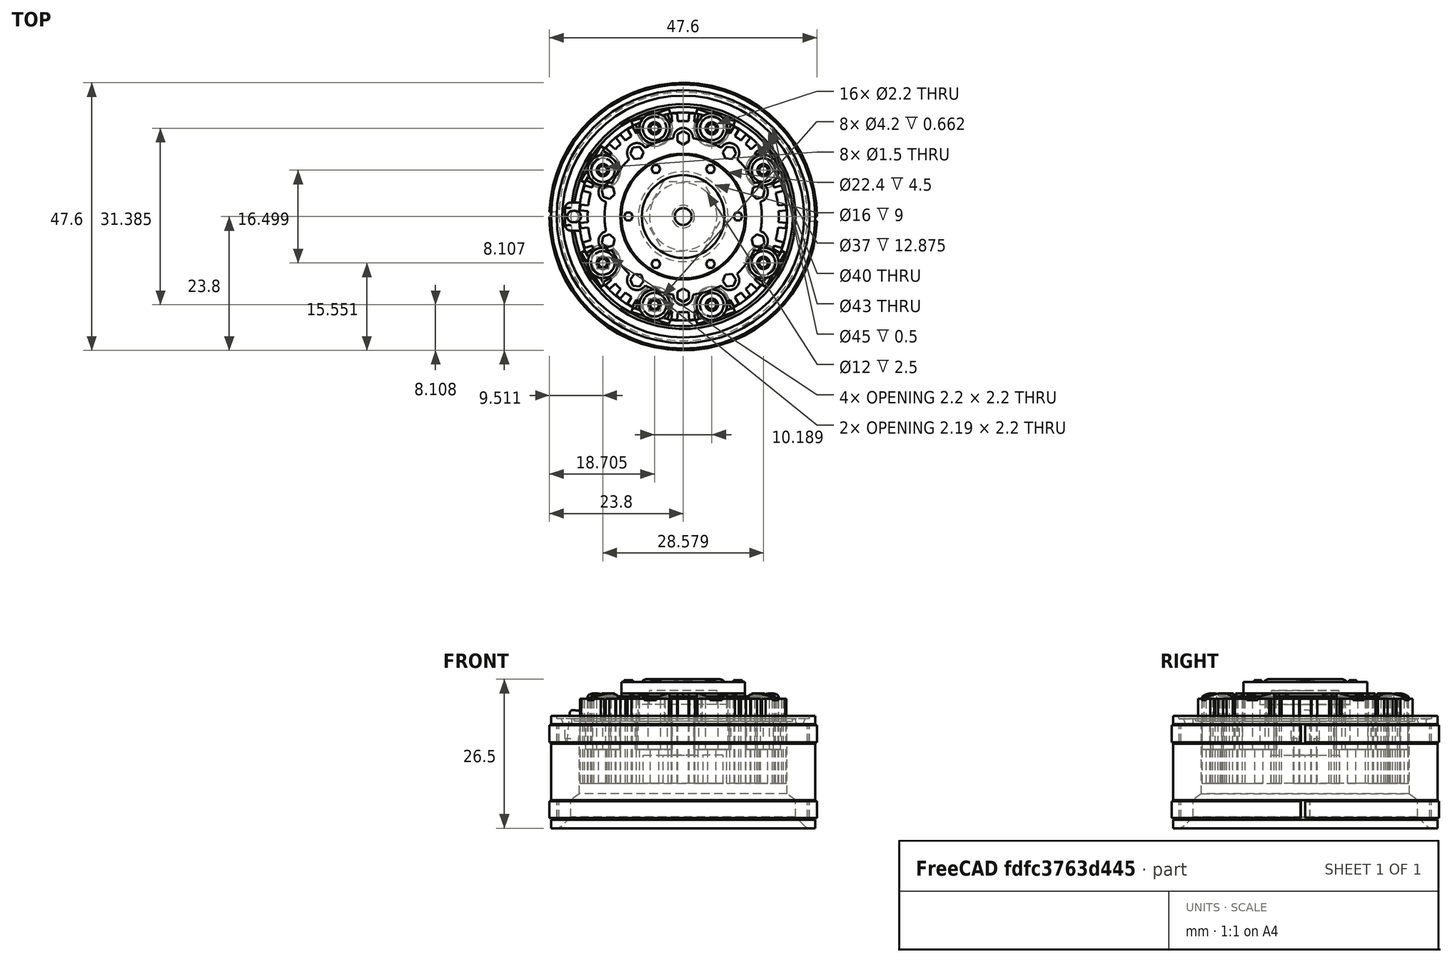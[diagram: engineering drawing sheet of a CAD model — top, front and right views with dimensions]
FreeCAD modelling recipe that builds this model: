
FCSTD DOCUMENT  (FreeCAD 0.18.4R)
Label: trilex_front_00
License: All rights reserved
LicenseURL: http://en.wikipedia.org/wiki/All_rights_reserved
objects: Part::Cylinder×99, Part::MultiFuse×80, Part::Box×60, Part::Cut×40, Part::Extrusion×17, Part::Feature×14, Part::RegularPolygon×10, Part::Fillet×7, Part::Chamfer×2, Part::Cone×1
note: 330 computed .brp shape members not serialized (recipe doc carries the construction recipe); baked Part::Feature solids carry a one-line shape summary decoded from their .brp

FEATURE [Part::Cylinder] Cylinder
  Angle = 360
  AttacherType = Attacher::AttachEngine3D
  Height = 20
  Radius = 23.5
FEATURE [Part::Cylinder] Cylinder002
  Angle = 360
  AttacherType = Attacher::AttachEngine3D
  Height = 17
  Radius = 22.1
FEATURE [Part::Cylinder] Cylinder001
  Angle = 360
  AttacherType = Attacher::AttachEngine3D
  Height = 17
  Radius = 23.5
FEATURE [Part::Cut] Cut
  Base = -> Cylinder001
  Placement = pos=(0,0,1.5) rot=(0,0,1;0rad)
  Refine = true
  Tool = -> Cylinder002
FEATURE [Part::Cut] Cut001
  Base = -> Cylinder
  Refine = true
  Tool = -> Cut
FEATURE [Part::Cylinder] Cylinder003
  Angle = 360
  AttacherType = Attacher::AttachEngine3D
  Height = 17
  Radius = 22
FEATURE [Part::Cylinder] Cylinder004
  Angle = 360
  AttacherType = Attacher::AttachEngine3D
  Height = 10
  Placement = pos=(0,0,0.5) rot=(0,0,1;0rad)
  Radius = 23.5
FEATURE [Part::Cut] Cut002
  Base = -> Cylinder004
  Placement = pos=(0,0,4.5) rot=(0,0,1;0rad)
  Refine = true
  Tool = -> Cylinder003
FEATURE [Part::Cylinder] Cylinder006
  Angle = 360
  AttacherType = Attacher::AttachEngine3D
  Height = 20
  Radius = 18.5
FEATURE [Part::Cylinder] Cylinder007
  Angle = 360
  AttacherType = Attacher::AttachEngine3D
  Height = 1
  Placement = pos=(0,0,19) rot=(0,0,1;0rad)
  Radius = 19.5
FEATURE [Part::Cylinder] Cylinder018
  Angle = 360
  AttacherType = Attacher::AttachEngine3D
  Height = 0.5
  Placement = pos=(0,0,19.5) rot=(0,0,1;0rad)
  Radius = 22.5
FEATURE [Part::Cylinder] Cylinder070
  Angle = 360
  AttacherType = Attacher::AttachEngine3D
  Height = 5
  Radius = 20
FEATURE [Part::MultiFuse] Fusion
  Refine = true
  Shapes = -> [Cut002,Cut001]
FEATURE [Part::Cut] Cut031
  Base = -> Fusion
  Refine = true
  Tool = -> Cylinder006
FEATURE [Part::Cut] Cut032
  Base = -> Cut031
  Refine = true
  Tool = -> Cylinder018
FEATURE [Part::Cut] Cut033
  Base = -> Cut032
  Refine = true
  Tool = -> Cylinder007
FEATURE [Part::Cut] Cut034
  Base = -> Cut033
  Refine = true
  Tool = -> Cylinder070
FEATURE [Part::Cylinder] Cylinder078
  Angle = 178
  AttacherType = Attacher::AttachEngine3D
  Height = 3
  Placement = pos=(0,0,1.8) rot=(0,0,1;0rad)
  Radius = 23.8
FEATURE [Part::Cylinder] Cylinder079
  Angle = 360
  AttacherType = Attacher::AttachEngine3D
  Height = 17
  Radius = 22.45
FEATURE [Part::Cut] Cut035
  Base = -> Cylinder078
  Refine = true
  Tool = -> Cylinder079
FEATURE [Part::Cylinder] Cylinder080
  Angle = 178
  AttacherType = Attacher::AttachEngine3D
  Height = 3
  Placement = pos=(0,0,1.8) rot=(0,0,1;0rad)
  Radius = 23.8
FEATURE [Part::Cylinder] Cylinder081
  Angle = 360
  AttacherType = Attacher::AttachEngine3D
  Height = 17
  Radius = 22.45
FEATURE [Part::Cut] Cut036
  Base = -> Cylinder080
  Placement = pos=(0,0,0) rot=(0,0,1;3.14159rad)
  Refine = true
  Tool = -> Cylinder081
FEATURE [Part::MultiFuse] Fusion032
  Placement = pos=(0,0,13.5) rot=(0,0,1;0rad)
  Refine = true
  Shapes = -> [Cut035,Cut036]
FEATURE [Part::Cut] Cut037
  Base = -> Cylinder080
  Placement = pos=(0,0,0) rot=(0,0,1;3.14159rad)
  Refine = true
  Tool = -> Cylinder081
FEATURE [Part::Cut] Cut038
  Base = -> Cylinder078
  Refine = true
  Tool = -> Cylinder079
FEATURE [Part::MultiFuse] Fusion033
  Refine = true
  Shapes = -> [Cut038,Cut037]
FEATURE [Part::MultiFuse] Fusion034  label="trilex-front-rim-support"
  Refine = true
  Shapes = -> [Fusion032,Fusion033]
FEATURE [Part::Cylinder] Cylinder163
  Angle = 360
  AttacherType = Attacher::AttachEngine3D
  Height = 5
  Placement = pos=(-16.5,0,14) rot=(0,0,1;0rad)
  Radius = 3.2
FEATURE [Part::Cone] Cone
  Angle = 360
  AttacherType = Attacher::AttachEngine3D
  Height = 6
  Placement = pos=(0,0,5) rot=(0,0,1;0rad)
  Radius1 = 20
  Radius2 = 12
FEATURE [Part::Cylinder] Cylinder164
  Angle = 360
  AttacherType = Attacher::AttachEngine3D
  Height = 5
  Placement = pos=(16.5,0,14) rot=(0,0,1;0rad)
  Radius = 3.2
FEATURE [Part::Cylinder] Cylinder102
  Angle = 360
  AttacherType = Attacher::AttachEngine3D
  Height = 11
  Placement = pos=(0,0,8) rot=(0,0,1;0rad)
  Radius = 17
FEATURE [Part::Cylinder] Cylinder104
  Angle = 360
  AttacherType = Attacher::AttachEngine3D
  Height = 5
  Placement = pos=(0,0,19) rot=(0,0,1;0rad)
  Radius = 11
FEATURE [Part::Cylinder] Cylinder077
  Angle = 360
  AttacherType = Attacher::AttachEngine3D
  Height = 10
  Placement = pos=(0,0,15) rot=(0,0,1;0rad)
  Radius = 8
FEATURE [Part::Cylinder] Cylinder110
  Angle = 360
  AttacherType = Attacher::AttachEngine3D
  Height = 17
  Placement = pos=(0,0,9) rot=(0,0,1;0rad)
  Radius = 2
FEATURE [Part::Feature] Face008
  shape: bbox 17.79 x 17.28 x 2e-07 mm, 1 faces, 0 solids (baked)
FEATURE [Part::Extrusion] Extrude007
  Base = -> Face008
  Dir = (0,0,6)
  DirMode = 0
  FaceMakerClass = Part::FaceMakerExtrusion
  LengthFwd = 0
  LengthRev = 0
  Placement = pos=(0,0,16) rot=(0,0,1;0rad)
  Solid = false
  Symmetric = false
FEATURE [Part::Cylinder] Cylinder111
  Angle = 360
  AttacherType = Attacher::AttachEngine3D
  Height = 4
  Placement = pos=(0,0,12) rot=(0,0,1;0rad)
  Radius = 10
FEATURE [Part::MultiFuse] Fusion045
  Placement = pos=(0,0,-9) rot=(0,0,1;0rad)
  Refine = true
  Shapes = -> [Extrude007,Cylinder111]
FEATURE [Part::Cylinder] Cylinder124
  Angle = 360
  AttacherType = Attacher::AttachEngine3D
  Height = 5
  Placement = pos=(16.5,0,15) rot=(0,0,1;0rad)
  Radius = 1.1
FEATURE [Part::Cylinder] Cylinder125
  Angle = 360
  AttacherType = Attacher::AttachEngine3D
  Height = 5
  Placement = pos=(16.5,0,15) rot=(0,0,1;0rad)
  Radius = 3
FEATURE [Part::Box] Box012  label="Cube012"
  AttacherType = Attacher::AttachEngine3D
  Height = 5
  Length = 3
  Placement = pos=(16.5,-3,15) rot=(0,0,1;0rad)
  Width = 6
FEATURE [Part::MultiFuse] Fusion052
  Refine = true
  Shapes = -> [Cylinder125,Box012]
FEATURE [Part::Cut] Cut061003
  Base = -> Fusion052
  Placement = pos=(0,0,-2) rot=(0,0,-1;0.523599rad)
  Refine = true
  Tool = -> Cylinder124
FEATURE [Part::Cylinder] Cylinder126
  Angle = 360
  AttacherType = Attacher::AttachEngine3D
  Height = 2
  Placement = pos=(0,0,19) rot=(0,0,1;0rad)
  Radius = 21.5
FEATURE [Part::Cylinder] Cylinder127
  Angle = 360
  AttacherType = Attacher::AttachEngine3D
  Height = 2
  Placement = pos=(0,0,19) rot=(0,0,1;0rad)
  Radius = 20
FEATURE [Part::Cut] Cut061004
  Base = -> Cylinder126
  Placement = pos=(0,0,-0.5) rot=(0,0,1;0rad)
  Refine = true
  Tool = -> Cylinder127
FEATURE [Part::Cut] Cut061005
  Base = -> Cut034
  Refine = true
  Tool = -> Cone
FEATURE [Part::Cut] Cut061006
  Base = -> Cut061005
  Refine = true
  Tool = -> Cut061004
FEATURE [Part::Box] Box013  label="Cube013"
  AttacherType = Attacher::AttachEngine3D
  Height = 5
  Length = 3
  Placement = pos=(16.5,-3,15) rot=(0,0,1;0rad)
  Width = 6
FEATURE [Part::Cylinder] Cylinder128
  Angle = 360
  AttacherType = Attacher::AttachEngine3D
  Height = 5
  Placement = pos=(16.5,0,15) rot=(0,0,1;0rad)
  Radius = 3
FEATURE [Part::MultiFuse] Fusion053
  Refine = true
  Shapes = -> [Cylinder128,Box013]
FEATURE [Part::Cylinder] Cylinder129
  Angle = 360
  AttacherType = Attacher::AttachEngine3D
  Height = 5
  Placement = pos=(16.5,0,15) rot=(0,0,1;0rad)
  Radius = 1.1
FEATURE [Part::Cut] Cut061007
  Base = -> Fusion053
  Placement = pos=(0,0,-2) rot=(0,0,1;0.523599rad)
  Refine = true
  Tool = -> Cylinder129
FEATURE [Part::Box] Box014  label="Cube014"
  AttacherType = Attacher::AttachEngine3D
  Height = 5
  Length = 3
  Placement = pos=(16.5,-3,15) rot=(0,0,1;0rad)
  Width = 6
FEATURE [Part::Cylinder] Cylinder130
  Angle = 360
  AttacherType = Attacher::AttachEngine3D
  Height = 5
  Placement = pos=(16.5,0,15) rot=(0,0,1;0rad)
  Radius = 3
FEATURE [Part::MultiFuse] Fusion054
  Refine = true
  Shapes = -> [Cylinder130,Box014]
FEATURE [Part::Cylinder] Cylinder131
  Angle = 360
  AttacherType = Attacher::AttachEngine3D
  Height = 5
  Placement = pos=(16.5,0,15) rot=(0,0,1;0rad)
  Radius = 1.1
FEATURE [Part::Cut] Cut061008
  Base = -> Fusion054
  Placement = pos=(0,0,-2) rot=(0,0,-1;1.25664rad)
  Refine = true
  Tool = -> Cylinder131
FEATURE [Part::Cylinder] Cylinder132
  Angle = 360
  AttacherType = Attacher::AttachEngine3D
  Height = 5
  Placement = pos=(16.5,0,15) rot=(0,0,1;0rad)
  Radius = 1.1
FEATURE [Part::Cylinder] Cylinder133
  Angle = 360
  AttacherType = Attacher::AttachEngine3D
  Height = 5
  Placement = pos=(16.5,0,15) rot=(0,0,1;0rad)
  Radius = 3
FEATURE [Part::Box] Box015  label="Cube015"
  AttacherType = Attacher::AttachEngine3D
  Height = 5
  Length = 3
  Placement = pos=(16.5,-3,15) rot=(0,0,1;0rad)
  Width = 6
FEATURE [Part::MultiFuse] Fusion055
  Refine = true
  Shapes = -> [Cylinder133,Box015]
FEATURE [Part::Cut] Cut061009
  Base = -> Fusion055
  Placement = pos=(0,0,-2) rot=(0,0,-1;1.88496rad)
  Refine = true
  Tool = -> Cylinder132
FEATURE [Part::Cylinder] Cylinder134
  Angle = 360
  AttacherType = Attacher::AttachEngine3D
  Height = 5
  Placement = pos=(16.5,0,15) rot=(0,0,1;0rad)
  Radius = 1.1
FEATURE [Part::Box] Box016  label="Cube016"
  AttacherType = Attacher::AttachEngine3D
  Height = 5
  Length = 3
  Placement = pos=(16.5,-3,15) rot=(0,0,1;0rad)
  Width = 6
FEATURE [Part::Cylinder] Cylinder135
  Angle = 360
  AttacherType = Attacher::AttachEngine3D
  Height = 5
  Placement = pos=(16.5,0,15) rot=(0,0,1;0rad)
  Radius = 3
FEATURE [Part::MultiFuse] Fusion056
  Refine = true
  Shapes = -> [Cylinder135,Box016]
FEATURE [Part::Cut] Cut061010
  Base = -> Fusion056
  Placement = pos=(0,0,-2) rot=(0,0,1;3.66519rad)
  Refine = true
  Tool = -> Cylinder134
FEATURE [Part::Cylinder] Cylinder136
  Angle = 360
  AttacherType = Attacher::AttachEngine3D
  Height = 5
  Placement = pos=(16.5,0,15) rot=(0,0,1;0rad)
  Radius = 3
FEATURE [Part::Box] Box017  label="Cube017"
  AttacherType = Attacher::AttachEngine3D
  Height = 5
  Length = 3
  Placement = pos=(16.5,-3,15) rot=(0,0,1;0rad)
  Width = 6
FEATURE [Part::Cylinder] Cylinder137
  Angle = 360
  AttacherType = Attacher::AttachEngine3D
  Height = 5
  Placement = pos=(16.5,0,15) rot=(0,0,1;0rad)
  Radius = 1.1
FEATURE [Part::MultiFuse] Fusion057
  Refine = true
  Shapes = -> [Cylinder136,Box017]
FEATURE [Part::Cut] Cut061011
  Base = -> Fusion057
  Placement = pos=(0,0,-2) rot=(0,0,1;1.25664rad)
  Refine = true
  Tool = -> Cylinder137
FEATURE [Part::Cylinder] Cylinder138
  Angle = 360
  AttacherType = Attacher::AttachEngine3D
  Height = 5
  Placement = pos=(16.5,0,15) rot=(0,0,1;0rad)
  Radius = 3
FEATURE [Part::Cylinder] Cylinder139
  Angle = 360
  AttacherType = Attacher::AttachEngine3D
  Height = 5
  Placement = pos=(16.5,0,15) rot=(0,0,1;0rad)
  Radius = 1.1
FEATURE [Part::Box] Box018  label="Cube018"
  AttacherType = Attacher::AttachEngine3D
  Height = 5
  Length = 3
  Placement = pos=(16.5,-3,15) rot=(0,0,1;0rad)
  Width = 6
FEATURE [Part::MultiFuse] Fusion058
  Refine = true
  Shapes = -> [Cylinder138,Box018]
FEATURE [Part::Cut] Cut061012
  Base = -> Fusion058
  Placement = pos=(0,0,-2) rot=(0,0,1;1.88496rad)
  Refine = true
  Tool = -> Cylinder139
FEATURE [Part::Cylinder] Cylinder140
  Angle = 360
  AttacherType = Attacher::AttachEngine3D
  Height = 5
  Placement = pos=(16.5,0,15) rot=(0,0,1;0rad)
  Radius = 3
FEATURE [Part::Box] Box019  label="Cube019"
  AttacherType = Attacher::AttachEngine3D
  Height = 5
  Length = 3
  Placement = pos=(16.5,-3,15) rot=(0,0,1;0rad)
  Width = 6
FEATURE [Part::MultiFuse] Fusion059
  Refine = true
  Shapes = -> [Cylinder140,Box019]
FEATURE [Part::Cylinder] Cylinder141
  Angle = 360
  AttacherType = Attacher::AttachEngine3D
  Height = 5
  Placement = pos=(16.5,0,15) rot=(0,0,1;0rad)
  Radius = 1.1
FEATURE [Part::Cut] Cut061013
  Base = -> Fusion059
  Placement = pos=(0,0,-2) rot=(0,0,1;2.61799rad)
  Refine = true
  Tool = -> Cylinder141
FEATURE [Part::MultiFuse] Fusion060
  Placement = pos=(0,0,1) rot=(0,0,1;0rad)
  Refine = true
  Shapes = -> [Cut061007,Cut061009,Cut061008,Cut061013,Cut061012,Cut061011,Cut061010,Cut061003]
FEATURE [Part::MultiFuse] Fusion061
  Refine = true
  Shapes = -> [Cut061006,Fusion060]
FEATURE [Part::Chamfer] Chamfer
  Base = -> Fusion061
  Edges = 1 edges r=2: [Edge17]
FEATURE [Part::Fillet] Fillet061
  Base = -> Chamfer
  Edges = 1 edges r=1.5: [Edge1]
FEATURE [Part::Fillet] Fillet062  label="trilex-front-rim_"
  Base = -> Fillet061
  Edges = 3 edges r=0.499: [Edge174,Edge177,Edge179]
FEATURE [Part::Cylinder] Cylinder142
  Angle = 360
  AttacherType = Attacher::AttachEngine3D
  Height = 6
  Placement = pos=(15.4,0,8) rot=(0,0,1;0rad)
  Radius = 3
FEATURE [Part::Cylinder] Cylinder143
  Angle = 360
  AttacherType = Attacher::AttachEngine3D
  Height = 6
  Placement = pos=(16.5,0,8) rot=(0,0,1;0rad)
  Radius = 0.75
FEATURE [Part::Cut] Cut061014
  Base = -> Cylinder142
  Placement = pos=(0,0,0) rot=(0,0,1;1.25664rad)
  Refine = true
  Tool = -> Cylinder143
FEATURE [Part::Cylinder] Cylinder144
  Angle = 360
  AttacherType = Attacher::AttachEngine3D
  Height = 6
  Placement = pos=(16.5,0,8) rot=(0,0,1;0rad)
  Radius = 0.75
FEATURE [Part::Cylinder] Cylinder145
  Angle = 360
  AttacherType = Attacher::AttachEngine3D
  Height = 6
  Placement = pos=(15.4,0,8) rot=(0,0,1;0rad)
  Radius = 3
FEATURE [Part::Cut] Cut061015
  Base = -> Cylinder145
  Placement = pos=(0,0,0) rot=(0,0,1;0.523599rad)
  Refine = true
  Tool = -> Cylinder144
FEATURE [Part::Cylinder] Cylinder146
  Angle = 360
  AttacherType = Attacher::AttachEngine3D
  Height = 6
  Placement = pos=(16.5,0,8) rot=(0,0,1;0rad)
  Radius = 0.75
FEATURE [Part::Cylinder] Cylinder147
  Angle = 360
  AttacherType = Attacher::AttachEngine3D
  Height = 6
  Placement = pos=(15.4,0,8) rot=(0,0,1;0rad)
  Radius = 3
FEATURE [Part::Cut] Cut061016
  Base = -> Cylinder147
  Placement = pos=(0,0,0) rot=(0,0,1;1.88496rad)
  Refine = true
  Tool = -> Cylinder146
FEATURE [Part::Cylinder] Cylinder148
  Angle = 360
  AttacherType = Attacher::AttachEngine3D
  Height = 6
  Placement = pos=(16.5,0,8) rot=(0,0,1;0rad)
  Radius = 0.75
FEATURE [Part::Cylinder] Cylinder149
  Angle = 360
  AttacherType = Attacher::AttachEngine3D
  Height = 6
  Placement = pos=(15.4,0,8) rot=(0,0,1;0rad)
  Radius = 3
FEATURE [Part::Cut] Cut061017
  Base = -> Cylinder149
  Placement = pos=(0,0,0) rot=(0,0,1;2.61799rad)
  Refine = true
  Tool = -> Cylinder148
FEATURE [Part::Cylinder] Cylinder150
  Angle = 360
  AttacherType = Attacher::AttachEngine3D
  Height = 6
  Placement = pos=(15.4,0,8) rot=(0,0,1;0rad)
  Radius = 3
FEATURE [Part::Cylinder] Cylinder151
  Angle = 360
  AttacherType = Attacher::AttachEngine3D
  Height = 6
  Placement = pos=(16.5,0,8) rot=(0,0,1;0rad)
  Radius = 0.75
FEATURE [Part::Cut] Cut061018
  Base = -> Cylinder150
  Placement = pos=(0,0,0) rot=(0,0,1;3.66519rad)
  Refine = true
  Tool = -> Cylinder151
FEATURE [Part::Cylinder] Cylinder152
  Angle = 360
  AttacherType = Attacher::AttachEngine3D
  Height = 6
  Placement = pos=(15.4,0,8) rot=(0,0,1;0rad)
  Radius = 3
FEATURE [Part::Cylinder] Cylinder153
  Angle = 360
  AttacherType = Attacher::AttachEngine3D
  Height = 6
  Placement = pos=(16.5,0,8) rot=(0,0,1;0rad)
  Radius = 0.75
FEATURE [Part::Cut] Cut061019
  Base = -> Cylinder152
  Placement = pos=(0,0,0) rot=(0,0,-1;1.88496rad)
  Refine = true
  Tool = -> Cylinder153
FEATURE [Part::Cylinder] Cylinder154
  Angle = 360
  AttacherType = Attacher::AttachEngine3D
  Height = 6
  Placement = pos=(16.5,0,8) rot=(0,0,1;0rad)
  Radius = 0.75
FEATURE [Part::Cylinder] Cylinder155
  Angle = 360
  AttacherType = Attacher::AttachEngine3D
  Height = 6
  Placement = pos=(15.4,0,8) rot=(0,0,1;0rad)
  Radius = 3
FEATURE [Part::Cut] Cut061020
  Base = -> Cylinder155
  Placement = pos=(0,0,0) rot=(0,0,-1;1.25664rad)
  Refine = true
  Tool = -> Cylinder154
FEATURE [Part::Cylinder] Cylinder156
  Angle = 360
  AttacherType = Attacher::AttachEngine3D
  Height = 6
  Placement = pos=(16.5,0,8) rot=(0,0,1;0rad)
  Radius = 0.75
FEATURE [Part::Cylinder] Cylinder157
  Angle = 360
  AttacherType = Attacher::AttachEngine3D
  Height = 6
  Placement = pos=(15.4,0,8) rot=(0,0,1;0rad)
  Radius = 3
FEATURE [Part::Cut] Cut061021
  Base = -> Cylinder157
  Placement = pos=(0,0,0) rot=(0,0,-1;0.523599rad)
  Refine = true
  Tool = -> Cylinder156
FEATURE [Part::MultiFuse] Fusion062
  Refine = true
  Shapes = -> [Cut061014,Cut061015,Cut061019,Cut061017,Cut061021,Cut061016,Cut061018,Cut061020]
FEATURE [Part::Cylinder] Cylinder158
  Angle = 360
  AttacherType = Attacher::AttachEngine3D
  Height = 5
  Placement = pos=(16.5,0,14) rot=(0,0,1;0rad)
  Radius = 3.2
FEATURE [Part::Cylinder] Cylinder159
  Angle = 360
  AttacherType = Attacher::AttachEngine3D
  Height = 5
  Placement = pos=(-16.5,0,14) rot=(0,0,1;0rad)
  Radius = 3.2
FEATURE [Part::MultiFuse] Fusion063
  Placement = pos=(0,0,0) rot=(0,0,1;0.523599rad)
  Refine = true
  Shapes = -> [Cylinder159,Cylinder158]
FEATURE [Part::Cylinder] Cylinder160
  Angle = 360
  AttacherType = Attacher::AttachEngine3D
  Height = 5
  Placement = pos=(16.5,0,14) rot=(0,0,1;0rad)
  Radius = 3.2
FEATURE [Part::Cylinder] Cylinder161
  Angle = 360
  AttacherType = Attacher::AttachEngine3D
  Height = 5
  Placement = pos=(-16.5,0,14) rot=(0,0,1;0rad)
  Radius = 3.2
FEATURE [Part::MultiFuse] Fusion064
  Placement = pos=(0,0,0) rot=(0,0,1;1.25664rad)
  Refine = true
  Shapes = -> [Cylinder161,Cylinder160]
FEATURE [Part::Cylinder] Cylinder162
  Angle = 360
  AttacherType = Attacher::AttachEngine3D
  Height = 5
  Placement = pos=(16.5,0,14) rot=(0,0,1;0rad)
  Radius = 3.2
FEATURE [Part::MultiFuse] Fusion065
  Placement = pos=(0,0,0) rot=(0,0,1;1.88496rad)
  Refine = true
  Shapes = -> [Cylinder163,Cylinder162]
FEATURE [Part::Cylinder] Cylinder224
  Angle = 360
  AttacherType = Attacher::AttachEngine3D
  Height = 1
  Placement = pos=(14,0,22.5) rot=(0,0,1;0rad)
  Radius = 1.75
FEATURE [Part::Cylinder] Cylinder165
  Angle = 360
  AttacherType = Attacher::AttachEngine3D
  Height = 5
  Placement = pos=(-16.5,0,14) rot=(0,0,1;0rad)
  Radius = 3.2
FEATURE [Part::MultiFuse] Fusion066
  Placement = pos=(0,0,0) rot=(0,0,1;2.61799rad)
  Refine = true
  Shapes = -> [Cylinder165,Cylinder164]
FEATURE [Part::MultiFuse] Fusion067
  Refine = true
  Shapes = -> [Fusion063,Fusion066,Fusion065,Fusion064]
FEATURE [Part::Cylinder] Cylinder166
  Angle = 360
  AttacherType = Attacher::AttachEngine3D
  Height = 6
  Placement = pos=(16.5,0,14) rot=(0,0,1;0rad)
  Radius = 0.75
FEATURE [Part::Cylinder] Cylinder167
  Angle = 360
  AttacherType = Attacher::AttachEngine3D
  Height = 6
  Placement = pos=(16.5,0,14) rot=(0,0,1;0rad)
  Radius = 0.75
FEATURE [Part::Cylinder] Cylinder168
  Angle = 360
  AttacherType = Attacher::AttachEngine3D
  Height = 6
  Placement = pos=(16.5,0,14) rot=(0,0,1;0rad)
  Radius = 0.75
FEATURE [Part::Cylinder] Cylinder169
  Angle = 360
  AttacherType = Attacher::AttachEngine3D
  Height = 6
  Placement = pos=(-16.5,0,14) rot=(0,0,1;0rad)
  Radius = 0.75
FEATURE [Part::MultiFuse] Fusion068
  Placement = pos=(0,0,0) rot=(0,0,1;0.523599rad)
  Refine = true
  Shapes = -> [Cylinder169,Cylinder166]
FEATURE [Part::Cylinder] Cylinder170
  Angle = 360
  AttacherType = Attacher::AttachEngine3D
  Height = 6
  Placement = pos=(16.5,0,14) rot=(0,0,1;0rad)
  Radius = 0.75
FEATURE [Part::Cylinder] Cylinder171
  Angle = 360
  AttacherType = Attacher::AttachEngine3D
  Height = 6
  Placement = pos=(-16.5,0,14) rot=(0,0,1;0rad)
  Radius = 0.75
FEATURE [Part::Cylinder] Cylinder172
  Angle = 360
  AttacherType = Attacher::AttachEngine3D
  Height = 6
  Placement = pos=(-16.5,0,14) rot=(0,0,1;0rad)
  Radius = 0.75
FEATURE [Part::Cylinder] Cylinder173
  Angle = 360
  AttacherType = Attacher::AttachEngine3D
  Height = 6
  Placement = pos=(-16.5,0,14) rot=(0,0,1;0rad)
  Radius = 0.75
FEATURE [Part::MultiFuse] Fusion070
  Placement = pos=(0,0,0) rot=(0,0,1;2.61799rad)
  Refine = true
  Shapes = -> [Cylinder173,Cylinder168]
FEATURE [Part::MultiFuse] Fusion071
  Placement = pos=(0,0,0) rot=(0,0,1;1.88496rad)
  Refine = true
  Shapes = -> [Cylinder171,Cylinder170]
FEATURE [Part::MultiFuse] Fusion072
  Placement = pos=(0,0,0) rot=(0,0,1;1.25664rad)
  Refine = true
  Shapes = -> [Cylinder172,Cylinder167]
FEATURE [Part::MultiFuse] Fusion069
  Placement = pos=(0,0,-6) rot=(0,0,1;0rad)
  Refine = true
  Shapes = -> [Fusion068,Fusion070,Fusion071,Fusion072]
FEATURE [Part::MultiFuse] Fusion073
  Refine = true
  Shapes = -> [Fusion069,Fusion067]
FEATURE [Part::Cut] Cut061022
  Base = -> Cylinder102
  Refine = true
  Tool = -> Fusion073
FEATURE [Part::MultiFuse] Fusion074
  Refine = true
  Shapes = -> [Cut061022,Fusion062]
FEATURE [Part::Box] Box020  label="Cube020"
  AttacherType = Attacher::AttachEngine3D
  Height = 11
  Length = 18.4
  Placement = pos=(-18.4,-0.5,8) rot=(0,0,1;0rad)
  Width = 1
FEATURE [Part::Box] Box021  label="Cube021"
  AttacherType = Attacher::AttachEngine3D
  Height = 11
  Length = 18.4
  Placement = pos=(0,-0.5,8) rot=(0,0,1;0rad)
  Width = 1
FEATURE [Part::MultiFuse] Fusion075
  Placement = pos=(0,0,0) rot=(0,0,1;0.279253rad)
  Refine = true
  Shapes = -> [Box021,Box020]
FEATURE [Part::Box] Box022  label="Cube022"
  AttacherType = Attacher::AttachEngine3D
  Height = 11
  Length = 18.4
  Placement = pos=(-18.4,-0.5,8) rot=(0,0,1;0rad)
  Width = 1
FEATURE [Part::Box] Box023  label="Cube023"
  AttacherType = Attacher::AttachEngine3D
  Height = 11
  Length = 18.4
  Placement = pos=(0,-0.5,8) rot=(0,0,1;0rad)
  Width = 1
FEATURE [Part::MultiFuse] Fusion076
  Placement = pos=(0,0,0) rot=(0,0,-1;0.279253rad)
  Refine = true
  Shapes = -> [Box023,Box022]
FEATURE [Part::Box] Box024  label="Cube024"
  AttacherType = Attacher::AttachEngine3D
  Height = 11
  Length = 18.4
  Placement = pos=(0,-0.5,8) rot=(0,0,1;0rad)
  Width = 1
FEATURE [Part::Box] Box025  label="Cube025"
  AttacherType = Attacher::AttachEngine3D
  Height = 11
  Length = 18.4
  Placement = pos=(-18.4,-0.5,8) rot=(0,0,1;0rad)
  Width = 1
FEATURE [Part::MultiFuse] Fusion077
  Placement = pos=(0,0,0) rot=(0,0,-1;0.087266rad)
  Refine = true
  Shapes = -> [Box024,Box025]
FEATURE [Part::Box] Box026  label="Cube026"
  AttacherType = Attacher::AttachEngine3D
  Height = 11
  Length = 18.4
  Placement = pos=(0,-0.5,8) rot=(0,0,1;0rad)
  Width = 1
FEATURE [Part::Box] Box027  label="Cube027"
  AttacherType = Attacher::AttachEngine3D
  Height = 11
  Length = 18.4
  Placement = pos=(-18.4,-0.5,8) rot=(0,0,1;0rad)
  Width = 1
FEATURE [Part::MultiFuse] Fusion078
  Placement = pos=(0,0,0) rot=(0,0,1;0.087266rad)
  Refine = true
  Shapes = -> [Box026,Box027]
FEATURE [Part::Box] Box028  label="Cube028"
  AttacherType = Attacher::AttachEngine3D
  Height = 11
  Length = 18.4
  Placement = pos=(-18.4,-0.5,8) rot=(0,0,1;0rad)
  Width = 1
FEATURE [Part::Box] Box029  label="Cube029"
  AttacherType = Attacher::AttachEngine3D
  Height = 11
  Length = 18.4
  Placement = pos=(0,-0.5,8) rot=(0,0,1;0rad)
  Width = 1
FEATURE [Part::MultiFuse] Fusion079
  Placement = pos=(0,0,0) rot=(0,0,1;1.65806rad)
  Refine = true
  Shapes = -> [Box029,Box028]
FEATURE [Part::Box] Box030  label="Cube030"
  AttacherType = Attacher::AttachEngine3D
  Height = 11
  Length = 18.4
  Placement = pos=(0,-0.5,8) rot=(0,0,1;0rad)
  Width = 1
FEATURE [Part::Box] Box031  label="Cube031"
  AttacherType = Attacher::AttachEngine3D
  Height = 11
  Length = 18.4
  Placement = pos=(-18.4,-0.5,8) rot=(0,0,1;0rad)
  Width = 1
FEATURE [Part::MultiFuse] Fusion080
  Placement = pos=(0,0,0) rot=(0,0,1;1.48353rad)
  Refine = true
  Shapes = -> [Box030,Box031]
FEATURE [Part::Box] Box032  label="Cube032"
  AttacherType = Attacher::AttachEngine3D
  Height = 11
  Length = 18.4
  Placement = pos=(-18.4,-0.5,8) rot=(0,0,1;0rad)
  Width = 1
FEATURE [Part::Box] Box033  label="Cube033"
  AttacherType = Attacher::AttachEngine3D
  Height = 11
  Length = 18.4
  Placement = pos=(0,-0.5,8) rot=(0,0,1;0rad)
  Width = 1
FEATURE [Part::MultiFuse] Fusion081
  Placement = pos=(0,0,0) rot=(0,0,1;0.750492rad)
  Refine = true
  Shapes = -> [Box033,Box032]
FEATURE [Part::Box] Box034  label="Cube034"
  AttacherType = Attacher::AttachEngine3D
  Height = 11
  Length = 18.4
  Placement = pos=(0,-0.5,8) rot=(0,0,1;0rad)
  Width = 1
FEATURE [Part::Box] Box035  label="Cube035"
  AttacherType = Attacher::AttachEngine3D
  Height = 11
  Length = 18.4
  Placement = pos=(-18.4,-0.5,8) rot=(0,0,1;0rad)
  Width = 1
FEATURE [Part::MultiFuse] Fusion082
  Placement = pos=(0,0,0) rot=(0,0,1;1.02974rad)
  Refine = true
  Shapes = -> [Box034,Box035]
FEATURE [Part::Box] Box036  label="Cube036"
  AttacherType = Attacher::AttachEngine3D
  Height = 11
  Length = 18.4
  Placement = pos=(0,-0.5,8) rot=(0,0,1;0rad)
  Width = 1
FEATURE [Part::Box] Box037  label="Cube037"
  AttacherType = Attacher::AttachEngine3D
  Height = 11
  Length = 18.4
  Placement = pos=(-18.4,-0.5,8) rot=(0,0,1;0rad)
  Width = 1
FEATURE [Part::MultiFuse] Fusion083
  Placement = pos=(0,0,0) rot=(0,0,1;0.890118rad)
  Refine = true
  Shapes = -> [Box036,Box037]
FEATURE [Part::Box] Box038  label="Cube038"
  AttacherType = Attacher::AttachEngine3D
  Height = 11
  Length = 18.4
  Placement = pos=(0,-0.5,8) rot=(0,0,1;0rad)
  Width = 1
FEATURE [Part::Box] Box039  label="Cube039"
  AttacherType = Attacher::AttachEngine3D
  Height = 11
  Length = 18.4
  Placement = pos=(-18.4,-0.5,8) rot=(0,0,1;0rad)
  Width = 1
FEATURE [Part::MultiFuse] Fusion084
  Placement = pos=(0,0,0) rot=(0,0,1;2.11185rad)
  Refine = true
  Shapes = -> [Box038,Box039]
FEATURE [Part::Box] Box040  label="Cube040"
  AttacherType = Attacher::AttachEngine3D
  Height = 11
  Length = 18.4
  Placement = pos=(-18.4,-0.5,8) rot=(0,0,1;0rad)
  Width = 1
FEATURE [Part::Box] Box041  label="Cube041"
  AttacherType = Attacher::AttachEngine3D
  Height = 11
  Length = 18.4
  Placement = pos=(0,-0.5,8) rot=(0,0,1;0rad)
  Width = 1
FEATURE [Part::MultiFuse] Fusion085
  Placement = pos=(0,0,0) rot=(0,0,1;2.3911rad)
  Refine = true
  Shapes = -> [Box041,Box040]
FEATURE [Part::Box] Box042  label="Cube042"
  AttacherType = Attacher::AttachEngine3D
  Height = 11
  Length = 18.4
  Placement = pos=(0,-0.5,8) rot=(0,0,1;0rad)
  Width = 1
FEATURE [Part::Box] Box043  label="Cube043"
  AttacherType = Attacher::AttachEngine3D
  Height = 11
  Length = 18.4
  Placement = pos=(-18.4,-0.5,8) rot=(0,0,1;0rad)
  Width = 1
FEATURE [Part::MultiFuse] Fusion086
  Placement = pos=(0,0,0) rot=(0,0,1;2.25148rad)
  Refine = true
  Shapes = -> [Box042,Box043]
FEATURE [Part::MultiFuse] Fusion087
  Refine = true
  Shapes = -> [Fusion075,Fusion078,Fusion086,Fusion081,Fusion082,Fusion079,Fusion080,Fusion085,Fusion076,Fusion084,Fusion083,Fusion077]
FEATURE [Part::MultiFuse] Fusion088
  Refine = true
  Shapes = -> [Fusion074,Fusion087]
FEATURE [Part::MultiFuse] Fusion089
  Refine = true
  Shapes = -> [Fusion088,Cylinder104]
FEATURE [Part::Cylinder] Cylinder174
  Angle = 360
  AttacherType = Attacher::AttachEngine3D
  Height = 2
  Placement = pos=(0,0,-6) rot=(0,0,1;0rad)
  Radius = 7.5
FEATURE [Part::Fillet] Fillet006
  Base = -> Cylinder174
  Edges = 1 edges r=1: [Edge1]
  Placement = pos=(0,0,-6) rot=(0,0,1;0rad)
FEATURE [Part::Cylinder] Cylinder175
  Angle = 360
  AttacherType = Attacher::AttachEngine3D
  Height = 0.3
  Placement = pos=(0,0,-10.3) rot=(0,0,1;0rad)
  Radius = 1.5
FEATURE [Part::Cut] Cut061023
  Base = -> Fillet006
  Refine = true
  Tool = -> Cylinder175
FEATURE [Part::Fillet] Fillet005
  Base = -> Cut061023
  Edges = 1 edges r=0.29: [Edge6]
  Placement = pos=(0,0,47.5) rot=(0,0,1;0rad)
FEATURE [Part::Cylinder] Cylinder176
  Angle = 360
  AttacherType = Attacher::AttachEngine3D
  Height = 2
  Placement = pos=(0,0,26) rot=(0,0,1;0rad)
  Radius = 11
FEATURE [Part::Cylinder] Cylinder177
  Angle = 360
  AttacherType = Attacher::AttachEngine3D
  Height = 2
  Placement = pos=(0,0,24) rot=(0,0,1;0rad)
  Radius = 8
FEATURE [Part::MultiFuse] Fusion093
  Refine = true
  Shapes = -> [Cylinder176,Cylinder177]
FEATURE [Part::Cylinder] Cylinder178
  Angle = 360
  AttacherType = Attacher::AttachEngine3D
  Height = 3.5
  Placement = pos=(0,0,24) rot=(0,0,1;0rad)
  Radius = 6
FEATURE [Part::Cut] Cut061024
  Base = -> Fusion093
  Placement = pos=(0,0,9) rot=(0,0,1;0rad)
  Refine = true
  Tool = -> Cylinder178
FEATURE [Part::Feature] Face009
  shape: bbox 1.791 x 1.578 x 2e-07 mm, 1 faces, 0 solids (baked)
FEATURE [Part::Extrusion] Extrude011
  Base = -> Face009
  Dir = (0,0,0.3)
  DirMode = 0
  FaceMakerClass = Part::FaceMakerExtrusion
  LengthFwd = 0
  LengthRev = 0
  Placement = pos=(-1.75,0,47.5) rot=(0,0,1;3.14159rad)
  Solid = false
  Symmetric = false
FEATURE [Part::Feature] Face010
  shape: bbox 1.791 x 1.578 x 2e-07 mm, 1 faces, 0 solids (baked)
FEATURE [Part::Extrusion] Extrude013
  Base = -> Face010
  Dir = (0,0,0.3)
  DirMode = 0
  FaceMakerClass = Part::FaceMakerExtrusion
  LengthFwd = 0
  LengthRev = 0
  Placement = pos=(-1.75,0,47.5) rot=(0,0,1;3.14159rad)
  Solid = false
  Symmetric = false
FEATURE [Part::Feature] Face006
  shape: bbox 1.791 x 1.578 x 2e-07 mm, 1 faces, 0 solids (baked)
FEATURE [Part::Extrusion] Extrude006
  Base = -> Face006
  Dir = (0,0,0.3)
  DirMode = 0
  FaceMakerClass = Part::FaceMakerExtrusion
  LengthFwd = 0
  LengthRev = 0
  Placement = pos=(1.75,0,47.5) rot=(0,0,1;0rad)
  Solid = false
  Symmetric = false
FEATURE [Part::MultiFuse] Fusion092
  Refine = true
  Shapes = -> [Extrude013,Extrude006]
FEATURE [Part::Feature] Face011
  shape: bbox 1.791 x 1.578 x 2e-07 mm, 1 faces, 0 solids (baked)
FEATURE [Part::Extrusion] Extrude012
  Base = -> Face011
  Dir = (0,0,0.3)
  DirMode = 0
  FaceMakerClass = Part::FaceMakerExtrusion
  LengthFwd = 0
  LengthRev = 0
  Placement = pos=(1.75,0,47.5) rot=(0,0,1;0rad)
  Solid = false
  Symmetric = false
FEATURE [Part::MultiFuse] Fusion091
  Placement = pos=(0,0,0) rot=(0,0,1;2.0944rad)
  Refine = true
  Shapes = -> [Extrude011,Extrude012]
FEATURE [Part::Feature] Face012
  shape: bbox 1.791 x 1.578 x 2e-07 mm, 1 faces, 0 solids (baked)
FEATURE [Part::Extrusion] Extrude009
  Base = -> Face012
  Dir = (0,0,0.3)
  DirMode = 0
  FaceMakerClass = Part::FaceMakerExtrusion
  LengthFwd = 0
  LengthRev = 0
  Placement = pos=(-1.75,0,47.5) rot=(0,0,1;3.14159rad)
  Solid = false
  Symmetric = false
FEATURE [Part::Feature] Face013
  shape: bbox 1.791 x 1.578 x 2e-07 mm, 1 faces, 0 solids (baked)
FEATURE [Part::Extrusion] Extrude010
  Base = -> Face013
  Dir = (0,0,0.3)
  DirMode = 0
  FaceMakerClass = Part::FaceMakerExtrusion
  LengthFwd = 0
  LengthRev = 0
  Placement = pos=(1.75,0,47.5) rot=(0,0,1;0rad)
  Solid = false
  Symmetric = false
FEATURE [Part::MultiFuse] Fusion090
  Placement = pos=(0,0,0) rot=(0,0,1;4.18879rad)
  Refine = true
  Shapes = -> [Extrude009,Extrude010]
FEATURE [Part::MultiFuse] Fusion094  label="trilex-front-cap"
  Placement = pos=(0,0,-11) rot=(0,0,1;0rad)
  Refine = true
  Shapes = -> [Fusion090,Cut061024,Fusion092,Fusion091,Fillet005]
FEATURE [Part::MultiFuse] Fusion095
  Refine = true
  Shapes = -> [Fusion045,Cylinder110,Cylinder077]
FEATURE [Part::Cut] Cut061025  label="trilex-front-hub-inner"
  Base = -> Fusion089
  Refine = true
  Tool = -> Fusion095
FEATURE [Part::Box] Box044  label="Cube044"
  AttacherType = Attacher::AttachEngine3D
  Height = 4
  Length = 18.4
  Placement = pos=(-18.4,-0.5,8) rot=(0,0,1;0rad)
  Width = 1
FEATURE [Part::Box] Box045  label="Cube045"
  AttacherType = Attacher::AttachEngine3D
  Height = 4
  Length = 18.4
  Placement = pos=(0,-0.5,8) rot=(0,0,1;0rad)
  Width = 1
FEATURE [Part::MultiFuse] Fusion096
  Placement = pos=(0,0,0) rot=(0,0,1;0.279253rad)
  Refine = true
  Shapes = -> [Box045,Box044]
FEATURE [Part::Box] Box046  label="Cube046"
  AttacherType = Attacher::AttachEngine3D
  Height = 4
  Length = 18.4
  Placement = pos=(-18.4,-0.5,8) rot=(0,0,1;0rad)
  Width = 1
FEATURE [Part::Box] Box047  label="Cube047"
  AttacherType = Attacher::AttachEngine3D
  Height = 4
  Length = 18.4
  Placement = pos=(0,-0.5,8) rot=(0,0,1;0rad)
  Width = 1
FEATURE [Part::MultiFuse] Fusion097
  Placement = pos=(0,0,0) rot=(0,0,-1;0.279253rad)
  Refine = true
  Shapes = -> [Box047,Box046]
FEATURE [Part::Box] Box048  label="Cube048"
  AttacherType = Attacher::AttachEngine3D
  Height = 4
  Length = 18.4
  Placement = pos=(0,-0.5,8) rot=(0,0,1;0rad)
  Width = 1
FEATURE [Part::Box] Box049  label="Cube049"
  AttacherType = Attacher::AttachEngine3D
  Height = 4
  Length = 18.4
  Placement = pos=(-18.4,-0.5,8) rot=(0,0,1;0rad)
  Width = 1
FEATURE [Part::MultiFuse] Fusion098
  Placement = pos=(0,0,0) rot=(0,0,-1;0.087266rad)
  Refine = true
  Shapes = -> [Box048,Box049]
FEATURE [Part::Box] Box050  label="Cube050"
  AttacherType = Attacher::AttachEngine3D
  Height = 4
  Length = 18.4
  Placement = pos=(0,-0.5,8) rot=(0,0,1;0rad)
  Width = 1
FEATURE [Part::Box] Box051  label="Cube051"
  AttacherType = Attacher::AttachEngine3D
  Height = 4
  Length = 18.4
  Placement = pos=(-18.4,-0.5,8) rot=(0,0,1;0rad)
  Width = 1
FEATURE [Part::MultiFuse] Fusion099
  Placement = pos=(0,0,0) rot=(0,0,1;0.087266rad)
  Refine = true
  Shapes = -> [Box050,Box051]
FEATURE [Part::Box] Box052  label="Cube052"
  AttacherType = Attacher::AttachEngine3D
  Height = 4
  Length = 18.4
  Placement = pos=(-18.4,-0.5,8) rot=(0,0,1;0rad)
  Width = 1
FEATURE [Part::Box] Box053  label="Cube053"
  AttacherType = Attacher::AttachEngine3D
  Height = 4
  Length = 18.4
  Placement = pos=(0,-0.5,8) rot=(0,0,1;0rad)
  Width = 1
FEATURE [Part::MultiFuse] Fusion100
  Placement = pos=(0,0,0) rot=(0,0,1;1.65806rad)
  Refine = true
  Shapes = -> [Box053,Box052]
FEATURE [Part::Box] Box054  label="Cube054"
  AttacherType = Attacher::AttachEngine3D
  Height = 4
  Length = 18.4
  Placement = pos=(0,-0.5,8) rot=(0,0,1;0rad)
  Width = 1
FEATURE [Part::Box] Box055  label="Cube055"
  AttacherType = Attacher::AttachEngine3D
  Height = 4
  Length = 18.4
  Placement = pos=(-18.4,-0.5,8) rot=(0,0,1;0rad)
  Width = 1
FEATURE [Part::MultiFuse] Fusion101
  Placement = pos=(0,0,0) rot=(0,0,1;1.48353rad)
  Refine = true
  Shapes = -> [Box054,Box055]
FEATURE [Part::Box] Box056  label="Cube056"
  AttacherType = Attacher::AttachEngine3D
  Height = 4
  Length = 18.4
  Placement = pos=(-18.4,-0.5,8) rot=(0,0,1;0rad)
  Width = 1
FEATURE [Part::Box] Box057  label="Cube057"
  AttacherType = Attacher::AttachEngine3D
  Height = 4
  Length = 18.4
  Placement = pos=(0,-0.5,8) rot=(0,0,1;0rad)
  Width = 1
FEATURE [Part::MultiFuse] Fusion102
  Placement = pos=(0,0,0) rot=(0,0,1;0.750492rad)
  Refine = true
  Shapes = -> [Box057,Box056]
FEATURE [Part::Box] Box058  label="Cube058"
  AttacherType = Attacher::AttachEngine3D
  Height = 4
  Length = 18.4
  Placement = pos=(0,-0.5,8) rot=(0,0,1;0rad)
  Width = 1
FEATURE [Part::Box] Box059  label="Cube059"
  AttacherType = Attacher::AttachEngine3D
  Height = 4
  Length = 18.4
  Placement = pos=(-18.4,-0.5,8) rot=(0,0,1;0rad)
  Width = 1
FEATURE [Part::MultiFuse] Fusion103
  Placement = pos=(0,0,0) rot=(0,0,1;1.02974rad)
  Refine = true
  Shapes = -> [Box058,Box059]
FEATURE [Part::Box] Box060  label="Cube060"
  AttacherType = Attacher::AttachEngine3D
  Height = 4
  Length = 18.4
  Placement = pos=(0,-0.5,8) rot=(0,0,1;0rad)
  Width = 1
FEATURE [Part::Box] Box061  label="Cube061"
  AttacherType = Attacher::AttachEngine3D
  Height = 4
  Length = 18.4
  Placement = pos=(-18.4,-0.5,8) rot=(0,0,1;0rad)
  Width = 1
FEATURE [Part::MultiFuse] Fusion104
  Placement = pos=(0,0,0) rot=(0,0,1;0.890118rad)
  Refine = true
  Shapes = -> [Box060,Box061]
FEATURE [Part::Box] Box062  label="Cube062"
  AttacherType = Attacher::AttachEngine3D
  Height = 4
  Length = 18.4
  Placement = pos=(0,-0.5,8) rot=(0,0,1;0rad)
  Width = 1
FEATURE [Part::Box] Box063  label="Cube063"
  AttacherType = Attacher::AttachEngine3D
  Height = 4
  Length = 18.4
  Placement = pos=(-18.4,-0.5,8) rot=(0,0,1;0rad)
  Width = 1
FEATURE [Part::MultiFuse] Fusion105
  Placement = pos=(0,0,0) rot=(0,0,1;2.11185rad)
  Refine = true
  Shapes = -> [Box062,Box063]
FEATURE [Part::Box] Box064  label="Cube064"
  AttacherType = Attacher::AttachEngine3D
  Height = 4
  Length = 18.4
  Placement = pos=(-18.4,-0.5,8) rot=(0,0,1;0rad)
  Width = 1
FEATURE [Part::Box] Box065  label="Cube065"
  AttacherType = Attacher::AttachEngine3D
  Height = 4
  Length = 18.4
  Placement = pos=(0,-0.5,8) rot=(0,0,1;0rad)
  Width = 1
FEATURE [Part::MultiFuse] Fusion106
  Placement = pos=(0,0,0) rot=(0,0,1;2.3911rad)
  Refine = true
  Shapes = -> [Box065,Box064]
FEATURE [Part::Box] Box066  label="Cube066"
  AttacherType = Attacher::AttachEngine3D
  Height = 4
  Length = 18.4
  Placement = pos=(0,-0.5,8) rot=(0,0,1;0rad)
  Width = 1
FEATURE [Part::Box] Box067  label="Cube067"
  AttacherType = Attacher::AttachEngine3D
  Height = 4
  Length = 18.4
  Placement = pos=(-18.4,-0.5,8) rot=(0,0,1;0rad)
  Width = 1
FEATURE [Part::MultiFuse] Fusion107
  Placement = pos=(0,0,0) rot=(0,0,1;2.25148rad)
  Refine = true
  Shapes = -> [Box066,Box067]
FEATURE [Part::MultiFuse] Fusion108
  Placement = pos=(0,0,11) rot=(0,0,1;0rad)
  Refine = true
  Shapes = -> [Fusion096,Fusion099,Fusion107,Fusion102,Fusion103,Fusion100,Fusion101,Fusion106,Fusion097,Fusion105,Fusion104,Fusion098]
FEATURE [Part::Cylinder] Cylinder179
  Angle = 360
  AttacherType = Attacher::AttachEngine3D
  Height = 4
  Placement = pos=(0,0,19) rot=(0,0,1;0rad)
  Radius = 17
FEATURE [Part::Cylinder] Cylinder180
  Angle = 360
  AttacherType = Attacher::AttachEngine3D
  Height = 0.5
  Placement = pos=(0,0,23) rot=(0,0,1;0rad)
  Radius = 14
FEATURE [Part::MultiFuse] Fusion109
  Refine = true
  Shapes = -> [Fusion108,Cylinder180,Cylinder179]
FEATURE [Part::Cylinder] Cylinder206
  Angle = 360
  AttacherType = Attacher::AttachEngine3D
  Height = 5
  Placement = pos=(15.5,0,15) rot=(0,0,1;0rad)
  Radius = 1.1
FEATURE [Part::Box] Box082  label="Cube082"
  AttacherType = Attacher::AttachEngine3D
  Height = 4
  Length = 0.75
  Placement = pos=(18.2,-3.5,15) rot=(0,0,1;0rad)
  Width = 7
FEATURE [Part::Cylinder] Cylinder210
  Angle = 360
  AttacherType = Attacher::AttachEngine3D
  Height = 10
  Placement = pos=(10,0,24.2) rot=(0,1,0;1.5708rad)
  Radius = 5
FEATURE [Part::Cylinder] Cylinder211
  Angle = 360
  AttacherType = Attacher::AttachEngine3D
  Height = 5
  Placement = pos=(16.5,0,15) rot=(0,0,1;0rad)
  Radius = 2.7
FEATURE [Part::Cylinder] Cylinder212
  Angle = 360
  AttacherType = Attacher::AttachEngine3D
  Height = 1
  Placement = pos=(15.5,0,19) rot=(0,0,1;0rad)
  Radius = 2.1
FEATURE [Part::Box] Box083  label="Cube083"
  AttacherType = Attacher::AttachEngine3D
  Height = 4
  Length = 2
  Placement = pos=(16.5,-2.4,15) rot=(0,0,1;0rad)
  Width = 4.8
FEATURE [Part::MultiFuse] Fusion125
  Refine = true
  Shapes = -> [Box083,Box082,Cylinder211]
FEATURE [Part::MultiFuse] Fusion126
  Placement = pos=(1,0,0) rot=(0,0,1;0rad)
  Refine = true
  Shapes = -> [Cylinder206,Cylinder212]
FEATURE [Part::Cut] Cut061041
  Base = -> Fusion125
  Refine = true
  Tool = -> Fusion126
FEATURE [Part::Cut] Cut061040
  Base = -> Cut061041
  Refine = true
  Tool = -> Cylinder210
FEATURE [Part::Cylinder] Cylinder213
  Angle = 360
  AttacherType = Attacher::AttachEngine3D
  Height = 5
  Placement = pos=(0,0,19) rot=(0,0,1;0rad)
  Radius = 11.2
FEATURE [Part::Cut] Cut061042
  Base = -> Fusion109
  Refine = true
  Tool = -> Cylinder213
FEATURE [Part::Cylinder] Cylinder214
  Angle = 360
  AttacherType = Attacher::AttachEngine3D
  Height = 6
  Placement = pos=(16.5,0,14) rot=(0,0,1;0rad)
  Radius = 1.1
FEATURE [Part::Cylinder] Cylinder215
  Angle = 360
  AttacherType = Attacher::AttachEngine3D
  Height = 6
  Placement = pos=(16.5,0,14) rot=(0,0,1;0rad)
  Radius = 1.1
FEATURE [Part::Cylinder] Cylinder216
  Angle = 360
  AttacherType = Attacher::AttachEngine3D
  Height = 6
  Placement = pos=(16.5,0,14) rot=(0,0,1;0rad)
  Radius = 1.1
FEATURE [Part::Cylinder] Cylinder217
  Angle = 360
  AttacherType = Attacher::AttachEngine3D
  Height = 6
  Placement = pos=(-16.5,0,14) rot=(0,0,1;0rad)
  Radius = 1.1
FEATURE [Part::MultiFuse] Fusion129
  Placement = pos=(0,0,0) rot=(0,0,1;0.523599rad)
  Refine = true
  Shapes = -> [Cylinder217,Cylinder214]
FEATURE [Part::Cylinder] Cylinder218
  Angle = 360
  AttacherType = Attacher::AttachEngine3D
  Height = 6
  Placement = pos=(16.5,0,14) rot=(0,0,1;0rad)
  Radius = 1.1
FEATURE [Part::Cylinder] Cylinder219
  Angle = 360
  AttacherType = Attacher::AttachEngine3D
  Height = 6
  Placement = pos=(-16.5,0,14) rot=(0,0,1;0rad)
  Radius = 1.1
FEATURE [Part::Cylinder] Cylinder220
  Angle = 360
  AttacherType = Attacher::AttachEngine3D
  Height = 6
  Placement = pos=(-16.5,0,14) rot=(0,0,1;0rad)
  Radius = 1.1
FEATURE [Part::Cylinder] Cylinder221
  Angle = 360
  AttacherType = Attacher::AttachEngine3D
  Height = 6
  Placement = pos=(-16.5,0,14) rot=(0,0,1;0rad)
  Radius = 1.1
FEATURE [Part::MultiFuse] Fusion131
  Placement = pos=(0,0,0) rot=(0,0,1;2.61799rad)
  Refine = true
  Shapes = -> [Cylinder221,Cylinder216]
FEATURE [Part::MultiFuse] Fusion132
  Placement = pos=(0,0,0) rot=(0,0,1;1.88496rad)
  Refine = true
  Shapes = -> [Cylinder219,Cylinder218]
FEATURE [Part::MultiFuse] Fusion133
  Placement = pos=(0,0,0) rot=(0,0,1;1.25664rad)
  Refine = true
  Shapes = -> [Cylinder220,Cylinder215]
FEATURE [Part::MultiFuse] Fusion130
  Placement = pos=(0,0,3) rot=(0,0,1;0rad)
  Refine = true
  Shapes = -> [Fusion129,Fusion131,Fusion132,Fusion133]
FEATURE [Part::RegularPolygon] RegularPolygon  label="Regular polygon"
  AttacherType = Attacher::AttachEngine3D
  Circumradius = 1.2
  Polygon = 6
FEATURE [Part::Cylinder] Cylinder222
  Angle = 360
  AttacherType = Attacher::AttachEngine3D
  Height = 1
  Placement = pos=(14,0,22.5) rot=(0,0,1;0rad)
  Radius = 1.75
FEATURE [Part::Extrusion] Extrude014
  Base = -> RegularPolygon
  Dir = (0,0,1)
  DirMode = 0
  FaceMakerClass = Part::FaceMakerBullseye
  LengthFwd = 1
  LengthRev = 0
  Placement = pos=(14,0,23) rot=(0,0,1;0rad)
  Solid = true
  Symmetric = false
FEATURE [Part::RegularPolygon] RegularPolygon001  label="Regular polygon001"
  AttacherType = Attacher::AttachEngine3D
  Circumradius = 1.2
  Polygon = 6
FEATURE [Part::Cylinder] Cylinder223
  Angle = 360
  AttacherType = Attacher::AttachEngine3D
  Height = 1
  Placement = pos=(-14,0,22.5) rot=(0,0,1;0rad)
  Radius = 1.75
FEATURE [Part::Extrusion] Extrude015
  Base = -> RegularPolygon001
  Dir = (0,0,1)
  DirMode = 0
  FaceMakerClass = Part::FaceMakerBullseye
  LengthFwd = 1
  LengthRev = 0
  Placement = pos=(-14,0,23) rot=(0,0,1;0rad)
  Solid = true
  Symmetric = false
FEATURE [Part::MultiFuse] Fusion135
  Refine = true
  Shapes = -> [Extrude015,Cylinder222,Cylinder223,Extrude014]
FEATURE [Part::RegularPolygon] RegularPolygon002  label="Regular polygon002"
  AttacherType = Attacher::AttachEngine3D
  Circumradius = 1.2
  Polygon = 6
FEATURE [Part::Extrusion] Extrude016
  Base = -> RegularPolygon002
  Dir = (0,0,1)
  DirMode = 0
  FaceMakerClass = Part::FaceMakerBullseye
  LengthFwd = 1
  LengthRev = 0
  Placement = pos=(-14,0,23) rot=(0,0,1;0rad)
  Solid = true
  Symmetric = false
FEATURE [Part::RegularPolygon] RegularPolygon003  label="Regular polygon003"
  AttacherType = Attacher::AttachEngine3D
  Circumradius = 1.2
  Polygon = 6
FEATURE [Part::Cylinder] Cylinder225
  Angle = 360
  AttacherType = Attacher::AttachEngine3D
  Height = 1
  Placement = pos=(-14,0,22.5) rot=(0,0,1;0rad)
  Radius = 1.75
FEATURE [Part::Extrusion] Extrude017
  Base = -> RegularPolygon003
  Dir = (0,0,1)
  DirMode = 0
  FaceMakerClass = Part::FaceMakerBullseye
  LengthFwd = 1
  LengthRev = 0
  Placement = pos=(14,0,23) rot=(0,0,1;0rad)
  Solid = true
  Symmetric = false
FEATURE [Part::MultiFuse] Fusion136
  Placement = pos=(0,0,0) rot=(0,0,1;0.628319rad)
  Refine = true
  Shapes = -> [Extrude016,Cylinder224,Cylinder225,Extrude017]
FEATURE [Part::Cylinder] Cylinder226
  Angle = 360
  AttacherType = Attacher::AttachEngine3D
  Height = 1
  Placement = pos=(14,0,22.5) rot=(0,0,1;0rad)
  Radius = 1.75
FEATURE [Part::Cylinder] Cylinder227
  Angle = 360
  AttacherType = Attacher::AttachEngine3D
  Height = 1
  Placement = pos=(-14,0,22.5) rot=(0,0,1;0rad)
  Radius = 1.75
FEATURE [Part::RegularPolygon] RegularPolygon004  label="Regular polygon004"
  AttacherType = Attacher::AttachEngine3D
  Circumradius = 1.2
  Polygon = 6
FEATURE [Part::RegularPolygon] RegularPolygon005  label="Regular polygon005"
  AttacherType = Attacher::AttachEngine3D
  Circumradius = 1.2
  Polygon = 6
FEATURE [Part::Extrusion] Extrude018
  Base = -> RegularPolygon005
  Dir = (0,0,1)
  DirMode = 0
  FaceMakerClass = Part::FaceMakerBullseye
  LengthFwd = 1
  LengthRev = 0
  Placement = pos=(14,0,23) rot=(0,0,1;0rad)
  Solid = true
  Symmetric = false
FEATURE [Part::Extrusion] Extrude019
  Base = -> RegularPolygon004
  Dir = (0,0,1)
  DirMode = 0
  FaceMakerClass = Part::FaceMakerBullseye
  LengthFwd = 1
  LengthRev = 0
  Placement = pos=(-14,0,23) rot=(0,0,1;0rad)
  Solid = true
  Symmetric = false
FEATURE [Part::MultiFuse] Fusion137
  Placement = pos=(0,0,0) rot=(0,0,1;1.25664rad)
  Refine = true
  Shapes = -> [Extrude019,Cylinder226,Cylinder227,Extrude018]
FEATURE [Part::RegularPolygon] RegularPolygon006  label="Regular polygon006"
  AttacherType = Attacher::AttachEngine3D
  Circumradius = 1.2
  Polygon = 6
FEATURE [Part::RegularPolygon] RegularPolygon007  label="Regular polygon007"
  AttacherType = Attacher::AttachEngine3D
  Circumradius = 1.2
  Polygon = 6
FEATURE [Part::Extrusion] Extrude020
  Base = -> RegularPolygon007
  Dir = (0,0,1)
  DirMode = 0
  FaceMakerClass = Part::FaceMakerBullseye
  LengthFwd = 1
  LengthRev = 0
  Placement = pos=(14,0,23) rot=(0,0,1;0rad)
  Solid = true
  Symmetric = false
FEATURE [Part::Cylinder] Cylinder228
  Angle = 360
  AttacherType = Attacher::AttachEngine3D
  Height = 1
  Placement = pos=(-14,0,22.5) rot=(0,0,1;0rad)
  Radius = 1.75
FEATURE [Part::Cylinder] Cylinder229
  Angle = 360
  AttacherType = Attacher::AttachEngine3D
  Height = 1
  Placement = pos=(14,0,22.5) rot=(0,0,1;0rad)
  Radius = 1.75
FEATURE [Part::Extrusion] Extrude021
  Base = -> RegularPolygon006
  Dir = (0,0,1)
  DirMode = 0
  FaceMakerClass = Part::FaceMakerBullseye
  LengthFwd = 1
  LengthRev = 0
  Placement = pos=(-14,0,23) rot=(0,0,1;0rad)
  Solid = true
  Symmetric = false
FEATURE [Part::MultiFuse] Fusion138
  Placement = pos=(0,0,0) rot=(0,0,1;1.88496rad)
  Refine = true
  Shapes = -> [Extrude021,Cylinder229,Cylinder228,Extrude020]
FEATURE [Part::Cylinder] Cylinder230
  Angle = 360
  AttacherType = Attacher::AttachEngine3D
  Height = 1
  Placement = pos=(14,0,22.5) rot=(0,0,1;0rad)
  Radius = 1.75
FEATURE [Part::RegularPolygon] RegularPolygon008  label="Regular polygon008"
  AttacherType = Attacher::AttachEngine3D
  Circumradius = 1.2
  Polygon = 6
FEATURE [Part::Extrusion] Extrude022
  Base = -> RegularPolygon008
  Dir = (0,0,1)
  DirMode = 0
  FaceMakerClass = Part::FaceMakerBullseye
  LengthFwd = 1
  LengthRev = 0
  Placement = pos=(-14,0,23) rot=(0,0,1;0rad)
  Solid = true
  Symmetric = false
FEATURE [Part::RegularPolygon] RegularPolygon009  label="Regular polygon009"
  AttacherType = Attacher::AttachEngine3D
  Circumradius = 1.2
  Polygon = 6
FEATURE [Part::Cylinder] Cylinder231
  Angle = 360
  AttacherType = Attacher::AttachEngine3D
  Height = 1
  Placement = pos=(-14,0,22.5) rot=(0,0,1;0rad)
  Radius = 1.75
FEATURE [Part::Extrusion] Extrude023
  Base = -> RegularPolygon009
  Dir = (0,0,1)
  DirMode = 0
  FaceMakerClass = Part::FaceMakerBullseye
  LengthFwd = 1
  LengthRev = 0
  Placement = pos=(14,0,23) rot=(0,0,1;0rad)
  Solid = true
  Symmetric = false
FEATURE [Part::MultiFuse] Fusion139
  Placement = pos=(0,0,0) rot=(0,0,1;2.51327rad)
  Refine = true
  Shapes = -> [Extrude022,Cylinder230,Cylinder231,Extrude023]
FEATURE [Part::MultiFuse] Fusion140
  Placement = pos=(0,0,0) rot=(0,0,1;0.314159rad)
  Refine = true
  Shapes = -> [Fusion139,Fusion135,Fusion138,Fusion137,Fusion136]
FEATURE [Part::Box] Box084  label="Cube084"
  AttacherType = Attacher::AttachEngine3D
  Height = 4
  Length = 0.75
  Placement = pos=(18.95,-3.5,15) rot=(0,0,1;0rad)
  Width = 7
FEATURE [Part::Chamfer] Chamfer001
  Base = -> Box084
  Edges = 1 edges r=0.25: [Edge2]
FEATURE [Part::Cut] Cut061043
  Base = -> Cut061040
  Placement = pos=(0,0,4) rot=(0,0,1;0.523599rad)
  Refine = true
  Tool = -> Chamfer001
FEATURE [Part::Cut] Cut061044
  Base = -> Cut061042
  Refine = true
  Tool = -> Fusion130
FEATURE [Part::MultiFuse] Fusion142
  Refine = true
  Shapes = -> [Fusion140,Cut061044]
FEATURE [Part::Feature] Cut061043001  label="Cut061045"
  Placement = pos=(0,0,4) rot=(0,0,1;1.25664rad)
  shape: bbox 7.488 x 6.814 x 4.992 mm, 16 faces (baked)
FEATURE [Part::Feature] Cut061043002  label="Cut061046"
  Placement = pos=(0,0,4) rot=(0,0,1;1.88496rad)
  shape: bbox 7.488 x 6.814 x 4.992 mm, 16 faces (baked)
FEATURE [Part::Feature] Cut061043003  label="Cut061047"
  Placement = pos=(0,0,4) rot=(0,0,1;3.66519rad)
  shape: bbox 7.56 x 7.945 x 4.992 mm, 16 faces (baked)
FEATURE [Part::Feature] Cut061043004  label="Cut061048"
  Placement = pos=(0,0,4) rot=(0,0,1;2.61799rad)
  shape: bbox 7.56 x 7.945 x 4.992 mm, 16 faces (baked)
FEATURE [Part::Feature] Cut061043005  label="Cut061049"
  Placement = pos=(0,0,4) rot=(0,0,-1;0.523599rad)
  shape: bbox 7.56 x 7.945 x 4.992 mm, 16 faces (baked)
FEATURE [Part::Feature] Cut061043006  label="Cut061050"
  Placement = pos=(0,0,4) rot=(0,0,-1;1.25664rad)
  shape: bbox 7.488 x 6.814 x 4.992 mm, 16 faces (baked)
FEATURE [Part::Feature] Cut061043007  label="Cut061051"
  Placement = pos=(0,0,4) rot=(0,0,-1;1.88496rad)
  shape: bbox 7.488 x 6.814 x 4.992 mm, 16 faces (baked)
FEATURE [Part::MultiFuse] Fusion143
  Refine = true
  Shapes = -> [Cut061043,Cut061043004,Cut061043003,Cut061043002,Cut061043001,Cut061043005,Cut061043006,Cut061043007]
FEATURE [Part::MultiFuse] Fusion144  label="trilex-front-hub-outer"
  Refine = true
  Shapes = -> [Fusion142,Fusion143]
FEATURE [Part::Box] Box  label="Cube"
  AttacherType = Attacher::AttachEngine3D
  Height = 5
  Length = 10
  Placement = pos=(-19,-2.5,15) rot=(0,0,1;0rad)
  Width = 5
FEATURE [Part::Fillet] Fillet
  Base = -> Box
  Edges = 3 edges r=1: [Edge1,Edge3,Edge4]
  Placement = pos=(-2,0,0) rot=(0,0,1;0rad)
FEATURE [Part::Cut] Cut061043008
  Base = -> Fillet062
  Refine = true
  Tool = -> Fillet
FEATURE [Part::Fillet] Fillet063
  Base = -> Cut061043008
  Edges = 2 edges r=0.9: [Edge6,Edge29]
FEATURE [Part::Cylinder] Cylinder232
  Angle = 360
  AttacherType = Attacher::AttachEngine3D
  Height = 10
  Placement = pos=(-20,0,11) rot=(0,1,0;0.087266rad)
  Radius = 1
FEATURE [Part::Fillet] Fillet064
  Base = -> Cylinder232
  Edges = 1 edges r=0.5: [Edge1]
FEATURE [Part::MultiFuse] Fusion145  label="trilex-front-rim"
  Refine = true
  Shapes = -> [Fillet064,Fillet063]
